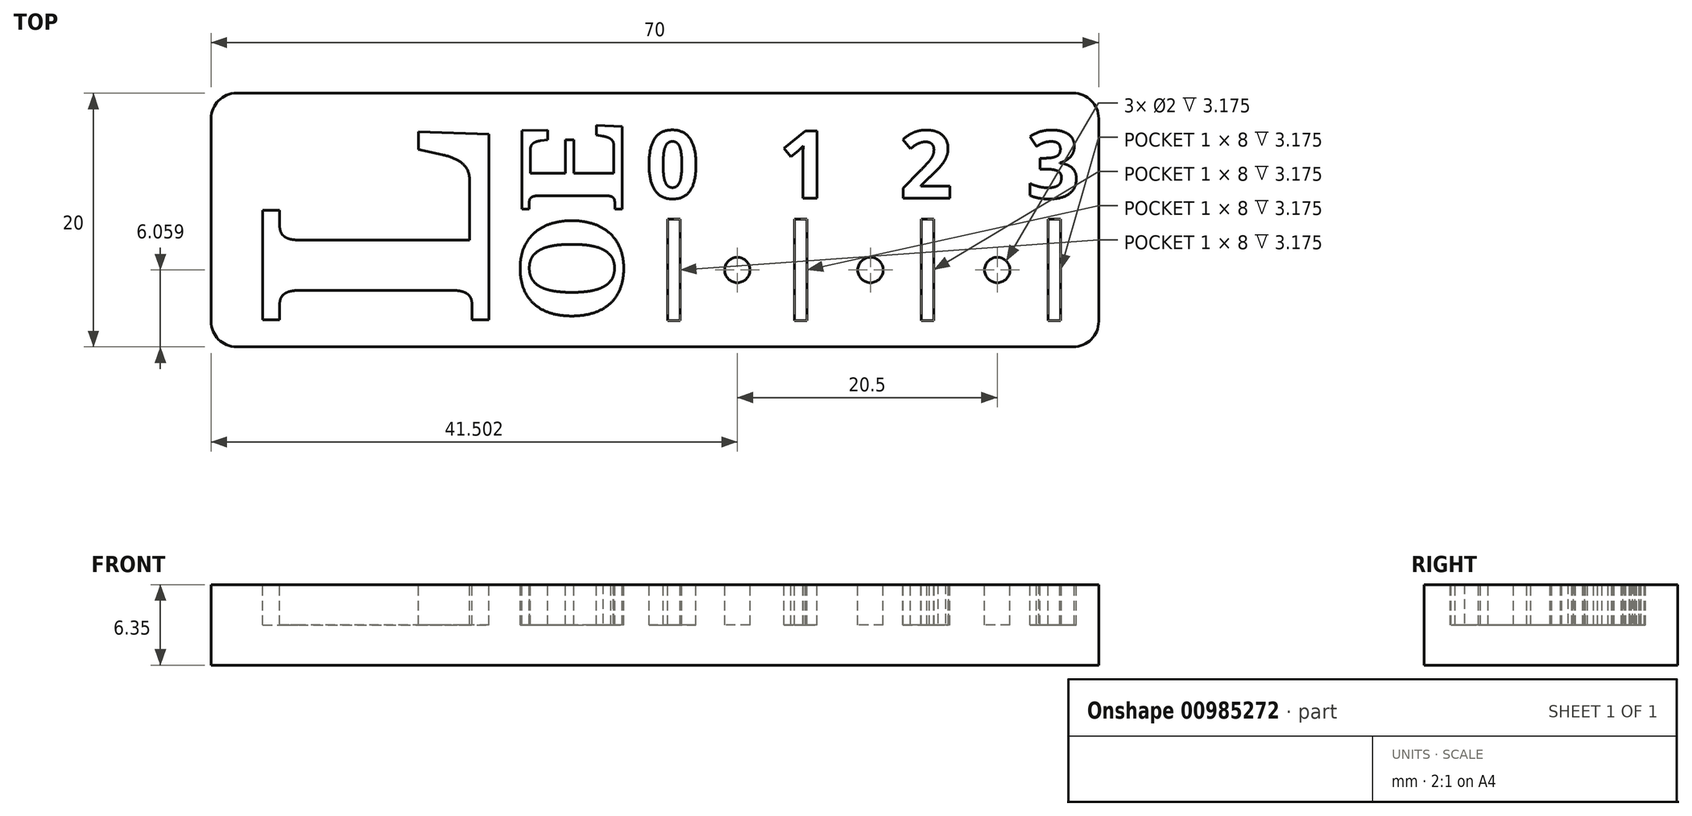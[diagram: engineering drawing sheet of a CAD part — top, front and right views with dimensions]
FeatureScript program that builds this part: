
annotation { "Feature Type Name" : "Feature", "Feature Type Description" : "" }
export const myFeature = defineFeature(function(context is Context, id is Id, definition is map)
    precondition{}
    {
        {
            var Q0;
            Q0=qCreatedBy(makeId("Top.planeOp"),FACE);
            var sketch = newSketch(context, id + "F0", { "sketchPlane" : qUnion([Q0])});
            skLineSegment(sketch, "E0.bottom", {"start": v(-55.27, 9.73) * mm, "end": v(10.73, 9.73) * mm});
            skLineSegment(sketch, "E0.top", {"start": v(-55.27, -10.27) * mm, "end": v(10.73, -10.27) * mm});
            skLineSegment(sketch, "E0.left", {"start": v(-57.27, 7.73) * mm, "end": v(-57.27, -8.27) * mm});
            skLineSegment(sketch, "E0.right", {"start": v(12.73, 7.73) * mm, "end": v(12.73, -8.27) * mm});
            skPoint(sketch, "E1.visualSharp", {"position": v(-57.27, 9.73) * mm});
            skArc(sketch, "E1.filletArc", {"start": v(-55.27, 9.73) * mm, "mid": v(-56.68, 9.15) * mm, "end": v(-57.27, 7.73) * mm});
            skPoint(sketch, "E2.visualSharp", {"position": v(12.73, 9.73) * mm});
            skArc(sketch, "E2.filletArc", {"start": v(12.73, 7.73) * mm, "mid": v(12.14, 9.15) * mm, "end": v(10.73, 9.73) * mm});
            skPoint(sketch, "E3.visualSharp", {"position": v(12.73, -10.27) * mm});
            skArc(sketch, "E3.filletArc", {"start": v(10.73, -10.27) * mm, "mid": v(12.14, -9.68) * mm, "end": v(12.73, -8.27) * mm});
            skPoint(sketch, "E4.visualSharp", {"position": v(-57.27, -10.27) * mm});
            skArc(sketch, "E4.filletArc", {"start": v(-57.27, -8.27) * mm, "mid": v(-56.68, -9.68) * mm, "end": v(-55.27, -10.27) * mm});
            skSolve(sketch);
        }
        {
            var Q0;
            Q0=qSketchRegion(id+"F0",true);
            extrude(context, id + "F1", {"entities" : qUnion([Q0]), "depth" : 6.35 * mm, "offsetDistance" : 25.4 * mm});
        }
        {
            var Q0;
            Q0=makeQuery(id+"F1.opExtrude","CAP_FACE",FACE,{"disambiguationData":[OSD([sQuery(id+"F0.wireOp",EDGE,"E0.bottom"),sQuery(id+"F0.wireOp",EDGE,"E0.top"),sQuery(id+"F0.wireOp",EDGE,"E0.left"),sQuery(id+"F0.wireOp",EDGE,"E0.right")])],"isStart":false});
            var sketch = newSketch(context, id + "F2", { "sketchPlane" : qUnion([Q0])});
            skText(sketch, "E5", { "text": "L", "fontName": "NotoSerif-Bold.ttf"});
            skText(sketch, "E6", { "text": "OE", "fontName": "NotoSerif-Bold.ttf"});
            skLineSegment(sketch, "E7.bottom", {"start": v(-21.27, -0.21) * mm, "end": v(-20.27, -0.21) * mm});
            skLineSegment(sketch, "E7.top", {"start": v(-21.27, -8.21) * mm, "end": v(-20.27, -8.21) * mm});
            skLineSegment(sketch, "E7.left", {"start": v(-21.27, -0.21) * mm, "end": v(-21.27, -8.21) * mm});
            skLineSegment(sketch, "E7.right", {"start": v(-20.27, -0.21) * mm, "end": v(-20.27, -8.21) * mm});
            skLineSegment(sketch, "E8.bottom", {"start": v(-11.27, -0.21) * mm, "end": v(-10.27, -0.21) * mm});
            skLineSegment(sketch, "E8.top", {"start": v(-11.27, -8.21) * mm, "end": v(-10.27, -8.21) * mm});
            skLineSegment(sketch, "E8.left", {"start": v(-11.27, -0.21) * mm, "end": v(-11.27, -8.21) * mm});
            skLineSegment(sketch, "E8.right", {"start": v(-10.27, -0.21) * mm, "end": v(-10.27, -8.21) * mm});
            skLineSegment(sketch, "E9.bottom", {"start": v(-1.27, -0.21) * mm, "end": v(-0.27, -0.21) * mm});
            skLineSegment(sketch, "E9.top", {"start": v(-1.27, -8.21) * mm, "end": v(-0.27, -8.21) * mm});
            skLineSegment(sketch, "E9.left", {"start": v(-1.27, -0.21) * mm, "end": v(-1.27, -8.21) * mm});
            skLineSegment(sketch, "E9.right", {"start": v(-0.27, -0.21) * mm, "end": v(-0.27, -8.21) * mm});
            skLineSegment(sketch, "E10.bottom", {"start": v(8.73, -0.21) * mm, "end": v(9.73, -0.21) * mm});
            skLineSegment(sketch, "E10.top", {"start": v(8.73, -8.21) * mm, "end": v(9.73, -8.21) * mm});
            skLineSegment(sketch, "E10.left", {"start": v(8.73, -0.21) * mm, "end": v(8.73, -8.21) * mm});
            skLineSegment(sketch, "E10.right", {"start": v(9.73, -0.21) * mm, "end": v(9.73, -8.21) * mm});
            skPoint(sketch, "E11", {"position": v(-20.77, -0.21) * mm});
            skPoint(sketch, "E12", {"position": v(-10.77, -0.21) * mm});
            skPoint(sketch, "E13", {"position": v(-0.77, -0.21) * mm});
            skCircle(sketch, "E14", {"center": v(-15.77, -4.21) * mm, "radius": 1 * mm});
            skPoint(sketch, "E15", {"position": v(-20.27, -4.21) * mm});
            skCircle(sketch, "E16", {"center": v(-5.27, -4.21) * mm, "radius": 1 * mm});
            skCircle(sketch, "E17", {"center": v(4.73, -4.21) * mm, "radius": 1 * mm});
            skPoint(sketch, "E18", {"position": v(-10.27, -4.21) * mm});
            skPoint(sketch, "E19", {"position": v(-0.27, -4.21) * mm});
            skText(sketch, "E20", { "text": "0", "fontName": "OpenSans-Bold.ttf"});
            skText(sketch, "E21", { "text": "1", "fontName": "OpenSans-Bold.ttf"});
            skText(sketch, "E22", { "text": "2", "fontName": "OpenSans-Bold.ttf"});
            skText(sketch, "E23", { "text": "3", "fontName": "OpenSans-Bold.ttf"});
            skPoint(sketch, "E24", {"position": v(-57.27, -0.27) * mm});
            const initialGuessF2  = {"E5": [-0.03535, -0.00884, 0, 1, 0.018], "E6": [-0.02484, -0.00845, 0, 1, 0.008], "E20": [-0.023, 0.00146, 1, 0, 0.00534], "E21": [-0.01254, 0.00146, 1, 0, 0.00534], "E22": [-0.003, 0.00146, 1, 0, 0.00534], "E23": [0.00702, 0.00146, 1, 0, 0.00534]};
            skSetInitialGuess(sketch, initialGuessF2);
            skSolve(sketch);
        }
        {
            var Q0;
            Q0=qSketchRegion(id+"F2",true);
            extrude(context, id + "F3", {"entities" : qUnion([Q0]), "operationType" : NewBodyOperationType.REMOVE, "oppositeDirection" : true, "depth" : 3.17 * mm, "offsetDistance" : 25.4 * mm});
        }
    });
